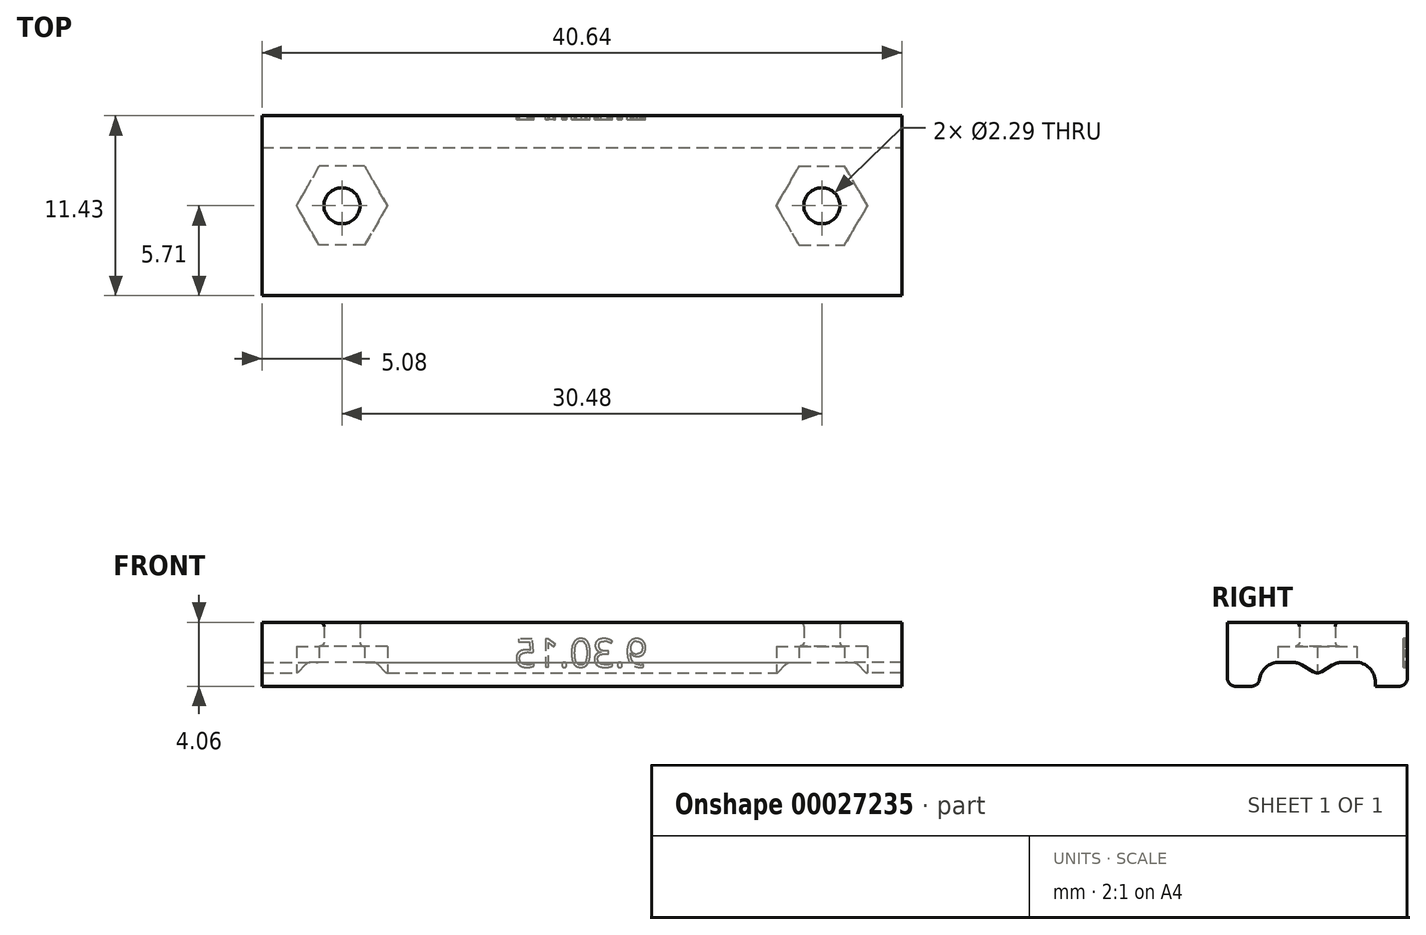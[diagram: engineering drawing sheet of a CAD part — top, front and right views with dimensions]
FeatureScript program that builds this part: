
annotation { "Feature Type Name" : "Feature", "Feature Type Description" : "" }
export const myFeature = defineFeature(function(context is Context, id is Id, definition is map)
    precondition{}
    {
        {
            var Q0;
            Q0=qCreatedBy(makeId("Right.planeOp"),FACE);
            var sketch = newSketch(context, id + "F0", { "sketchPlane" : qUnion([Q0])});
            skLineSegment(sketch, "E0", {"start": v(-5.71, 0) * mm, "end": v(5.71, 0) * mm});
            skLineSegment(sketch, "E1", {"start": v(5.72, 0) * mm, "end": v(5.72, 4.06) * mm});
            skLineSegment(sketch, "E2", {"start": v(5.71, 4.06) * mm, "end": v(-5.71, 4.06) * mm});
            skLineSegment(sketch, "E3", {"start": v(-5.71, 4.06) * mm, "end": v(-5.71, 0) * mm});
            skSolve(sketch);
        }
        {
            var Q0;
            Q0 = qSketchRegion(id + "F0", true);
            extrude(context, id + "F1", {"entities" : qUnion([Q0]), "oppositeDirection" : true, "depth" : 20.32 * mm});
        }
        {
            var Q0;
            Q0=qCreatedBy(makeId("Right.planeOp"),FACE);
            var sketch = newSketch(context, id + "F2", { "sketchPlane" : qUnion([Q0])});
            skLineSegment(sketch, "E4", {"start": v(-3.68, 0) * mm, "end": v(3.68, 0) * mm});
            skLineSegment(sketch, "E5", {"start": v(3.68, 0) * mm, "end": v(3.68, 1.52) * mm});
            skLineSegment(sketch, "E6", {"start": v(3.68, 1.52) * mm, "end": v(1.27, 1.52) * mm});
            skLineSegment(sketch, "E7", {"start": v(1.27, 1.52) * mm, "end": v(0, 0.76) * mm});
            skLineSegment(sketch, "E8", {"start": v(0, 0.76) * mm, "end": v(-1.27, 1.52) * mm});
            skLineSegment(sketch, "E9", {"start": v(-1.27, 1.52) * mm, "end": v(-3.68, 1.52) * mm});
            skLineSegment(sketch, "E10", {"start": v(-3.68, 1.52) * mm, "end": v(-3.68, 0) * mm});
            skLineSegment(sketch, "E11", {"start": v(-3.68, 0) * mm, "end": v(-5.71, 0) * mm, "construction": true});
            skLineSegment(sketch, "E12", {"start": v(3.68, 0) * mm, "end": v(5.72, 0) * mm, "construction": true});
            skSolve(sketch);
        }
        {
            var Q0;
            Q0 = qSketchRegion(id + "F2", true);
            extrude(context, id + "F3", {"entities" : qUnion([Q0]), "operationType" : NewBodyOperationType.REMOVE, "endBound" : BoundingType.THROUGH_ALL, "oppositeDirection" : true, "depth" : 19.05 * mm});
        }
        {
            var Q0;
            Q0=makeQuery(id+"F3.boolean.opBoolean","COPY",EDGE,{"derivedFrom":makeQuery(id+"F3.opExtrude","SWEPT_EDGE",EDGE,{"disambiguationData":[OSD([sQuery(id+"F2.wireOp",EDGE,"E5"),sQuery(id+"F2.wireOp",EDGE,"E6")])]})});
            var Q1;
            Q1=makeQuery(id+"F3.boolean.opBoolean","COPY",EDGE,{"derivedFrom":makeQuery(id+"F3.opExtrude","SWEPT_EDGE",EDGE,{"disambiguationData":[OSD([sQuery(id+"F2.wireOp",EDGE,"E9"),sQuery(id+"F2.wireOp",EDGE,"E10")])]})});
            fillet(context, id + "F4", {"entities" : qUnion([Q0, Q1]), "radius" : 1.27 * mm, "tangentPropagation" : true, "allowEdgeOverflow" : false});
        }
        {
            var Q0;
            Q0=makeQuery(id+"F3.boolean.opBoolean","COPY",EDGE,{"derivedFrom":makeQuery(id+"F3.opExtrude","SWEPT_EDGE",EDGE,{"disambiguationData":[OSD([sQuery(id+"F2.wireOp",EDGE,"E6"),sQuery(id+"F2.wireOp",EDGE,"E7")])]})});
            var Q1;
            Q1=makeQuery(id+"F3.boolean.opBoolean","COPY",EDGE,{"derivedFrom":makeQuery(id+"F3.opExtrude","SWEPT_EDGE",EDGE,{"disambiguationData":[OSD([sQuery(id+"F2.wireOp",EDGE,"E8"),sQuery(id+"F2.wireOp",EDGE,"E9")])]})});
            fillet(context, id + "F5", {"entities" : qUnion([Q0, Q1]), "radius" : 1.27 * mm, "tangentPropagation" : true, "allowEdgeOverflow" : false});
        }
        {
            var Q0;
            Q0=makeQuery(id+"F3.boolean.opBoolean","COPY",EDGE,{"derivedFrom":makeQuery(id+"F3.opExtrude","SWEPT_EDGE",EDGE,{"disambiguationData":[OSD([sQuery(id+"F2.wireOp",EDGE,"E7"),sQuery(id+"F2.wireOp",EDGE,"E8")])]})});
            fillet(context, id + "F6", {"entities" : qUnion([Q0]), "radius" : 0.5 * mm, "tangentPropagation" : true, "allowEdgeOverflow" : false});
        }
        {
            var Q0;
            Q0=makeQuery(id+"F3.boolean.opBoolean","COPY",EDGE,{"derivedFrom":makeQuery(id+"F3.opExtrude","SWEPT_EDGE",EDGE,{"disambiguationData":[OSD([sQuery(id+"F2.wireOp",EDGE,"E4"),sQuery(id+"F2.wireOp",EDGE,"E5")])]})});
            var Q1;
            Q1=makeQuery(id+"F1.opExtrude","SWEPT_EDGE",EDGE,{"disambiguationData":[OSD([sQuery(id+"F0.wireOp",EDGE,"E0"),sQuery(id+"F0.wireOp",EDGE,"E1")])]});
            var Q2;
            Q2=makeQuery(id+"F1.opExtrude","SWEPT_EDGE",EDGE,{"disambiguationData":[OSD([sQuery(id+"F0.wireOp",EDGE,"E0"),sQuery(id+"F0.wireOp",EDGE,"E3")])]});
            var Q3;
            Q3=makeQuery(id+"F3.boolean.opBoolean","COPY",EDGE,{"derivedFrom":makeQuery(id+"F3.opExtrude","SWEPT_EDGE",EDGE,{"disambiguationData":[OSD([sQuery(id+"F2.wireOp",EDGE,"E4"),sQuery(id+"F2.wireOp",EDGE,"E10")])]})});
            fillet(context, id + "F7", {"entities" : qUnion([Q0, Q1, Q2, Q3]), "radius" : 0.5 * mm, "tangentPropagation" : true, "allowEdgeOverflow" : false});
        }
        {
            var Q0;
            Q0=qCreatedBy(makeId("Top.planeOp"),FACE);
            var sketch = newSketch(context, id + "F8", { "sketchPlane" : qUnion([Q0])});
            skCircle(sketch, "E13.cCircle", {"center": v(-15.24, 0) * mm, "radius": 2.5 * mm, "construction": true});
            skLineSegment(sketch, "E13.0", {"start": v(-18.14, 0) * mm, "end": v(-16.69, 2.5) * mm});
            skLineSegment(sketch, "E13.1", {"start": v(-16.69, 2.5) * mm, "end": v(-13.8, 2.5) * mm});
            skLineSegment(sketch, "E13.2", {"start": v(-13.8, 2.5) * mm, "end": v(-12.34, 0) * mm});
            skLineSegment(sketch, "E13.3", {"start": v(-12.34, 0) * mm, "end": v(-13.8, -2.5) * mm});
            skLineSegment(sketch, "E13.4", {"start": v(-13.8, -2.5) * mm, "end": v(-16.69, -2.5) * mm});
            skLineSegment(sketch, "E13.5", {"start": v(-16.69, -2.5) * mm, "end": v(-18.14, 0) * mm});
            skPoint(sketch, "E13.0.midPoint", {"position": v(-17.41, 1.25) * mm});
            skLineSegment(sketch, "E14", {"start": v(-15.24, 0) * mm, "end": v(0, 0) * mm, "construction": true});
            skSolve(sketch);
        }
        {
            var Q0;
            Q0 = qSketchRegion(id + "F8", true);
            extrude(context, id + "F9", {"entities" : qUnion([Q0]), "operationType" : NewBodyOperationType.REMOVE, "depth" : 2.54 * mm});
        }
        {
            var Q0;
            Q0=qCreatedBy(makeId("Top.planeOp"),FACE);
            var sketch = newSketch(context, id + "F10", { "sketchPlane" : qUnion([Q0])});
            skCircle(sketch, "E15", {"center": v(-15.24, 0) * mm, "radius": 1.14 * mm});
            skSolve(sketch);
        }
        {
            var Q0;
            Q0 = qSketchRegion(id + "F10", true);
            extrude(context, id + "F11", {"entities" : qUnion([Q0]), "operationType" : NewBodyOperationType.REMOVE, "endBound" : BoundingType.THROUGH_ALL, "depth" : 25.4 * mm});
        }
        {
            var Q0;
            Q0=makeQuery(id+"F1.opExtrude","SWEPT_BODY",BODY,{"disambiguationData":[OSD([sQuery(id+"F0.wireOp",EDGE,"E0"),sQuery(id+"F0.wireOp",EDGE,"E1"),sQuery(id+"F0.wireOp",EDGE,"E2"),sQuery(id+"F0.wireOp",EDGE,"E3")])]});
            var Q1;
            Q1=qCreatedBy(makeId("Right.planeOp"),FACE);
            mirror(context, id + "F12", {"operationType" : NewBodyOperationType.ADD, "entities" : qUnion([Q0]), "mirrorPlane" : qUnion([Q1])});
        }
        {
            var Q0;
            Q0=makeQuery(id+"F12.opPattern","COPY",EDGE,{"derivedFrom":makeQuery(id+"F11.boolean.opBoolean","INTERSECT",EDGE,{"derivedFrom":[makeQuery(id+"F9.boolean.opBoolean","COPY",FACE,{"derivedFrom":makeQuery(id+"F9.opExtrude","CAP_FACE",FACE,{"disambiguationData":[OSD([sQuery(id+"F8.wireOp",EDGE,"E13.0"),sQuery(id+"F8.wireOp",EDGE,"E13.1"),sQuery(id+"F8.wireOp",EDGE,"E13.2"),sQuery(id+"F8.wireOp",EDGE,"E13.3"),sQuery(id+"F8.wireOp",EDGE,"E13.4"),sQuery(id+"F8.wireOp",EDGE,"E13.5")])],"isStart":false})}),makeQuery(id+"F11.opExtrude","SWEPT_FACE",FACE,{"disambiguationData":[OSD([sQuery(id+"F10.wireOp",EDGE,"E15")])]})]}),"instanceName":"1"});
            var Q1;
            Q1=makeQuery(id+"F12.opPattern","COPY",EDGE,{"derivedFrom":makeQuery(id+"F11.boolean.opBoolean","INTERSECT",EDGE,{"derivedFrom":[makeQuery(id+"F1.opExtrude","SWEPT_FACE",FACE,{"disambiguationData":[OSD([sQuery(id+"F0.wireOp",EDGE,"E2")])]}),makeQuery(id+"F11.opExtrude","SWEPT_FACE",FACE,{"disambiguationData":[OSD([sQuery(id+"F10.wireOp",EDGE,"E15")])]})]}),"instanceName":"1"});
            var Q2;
            Q2=makeQuery(id+"F11.boolean.opBoolean","INTERSECT",EDGE,{"derivedFrom":[makeQuery(id+"F9.boolean.opBoolean","COPY",FACE,{"derivedFrom":makeQuery(id+"F9.opExtrude","CAP_FACE",FACE,{"disambiguationData":[OSD([sQuery(id+"F8.wireOp",EDGE,"E13.0"),sQuery(id+"F8.wireOp",EDGE,"E13.1"),sQuery(id+"F8.wireOp",EDGE,"E13.2"),sQuery(id+"F8.wireOp",EDGE,"E13.3"),sQuery(id+"F8.wireOp",EDGE,"E13.4"),sQuery(id+"F8.wireOp",EDGE,"E13.5")])],"isStart":false})}),makeQuery(id+"F11.opExtrude","SWEPT_FACE",FACE,{"disambiguationData":[OSD([sQuery(id+"F10.wireOp",EDGE,"E15")])]})]});
            var Q3;
            Q3=makeQuery(id+"F11.boolean.opBoolean","INTERSECT",EDGE,{"derivedFrom":[makeQuery(id+"F1.opExtrude","SWEPT_FACE",FACE,{"disambiguationData":[OSD([sQuery(id+"F0.wireOp",EDGE,"E2")])]}),makeQuery(id+"F11.opExtrude","SWEPT_FACE",FACE,{"disambiguationData":[OSD([sQuery(id+"F10.wireOp",EDGE,"E15")])]})]});
            fillet(context, id + "F13", {"entities" : qUnion([Q0, Q1, Q2, Q3]), "radius" : 0.25 * mm, "tangentPropagation" : true, "allowEdgeOverflow" : false});
        }
        {
            var Q0;
            {var subQ0=makeQuery(id+"F1.opExtrude","SWEPT_FACE",FACE,{"disambiguationData":[OSD([sQuery(id+"F0.wireOp",EDGE,"E1")])]});Q0=makeQuery(id+"F12.boolean.opBoolean","MERGE",FACE,{"derivedFrom":[subQ0,makeQuery(id+"F12.opPattern","COPY",FACE,{"derivedFrom":subQ0,"instanceName":"1"})]});}
            var sketch = newSketch(context, id + "F14", { "sketchPlane" : qUnion([Q0])});
            skText(sketch, "E16", { "text": "9.30.15", "fontName": "OpenSans-Regular.ttf"});
            const initialGuessF14  = {"E16": [-0.00417, 0.00122, 1, 0, 0.0018]};
            skSetInitialGuess(sketch, initialGuessF14);
            skSolve(sketch);
        }
        {
            var Q0;
            Q0 = qSketchRegion(id + "F14", true);
            extrude(context, id + "F15", {"entities" : qUnion([Q0]), "operationType" : NewBodyOperationType.REMOVE, "oppositeDirection" : true, "depth" : 0.25 * mm});
        }
    });
